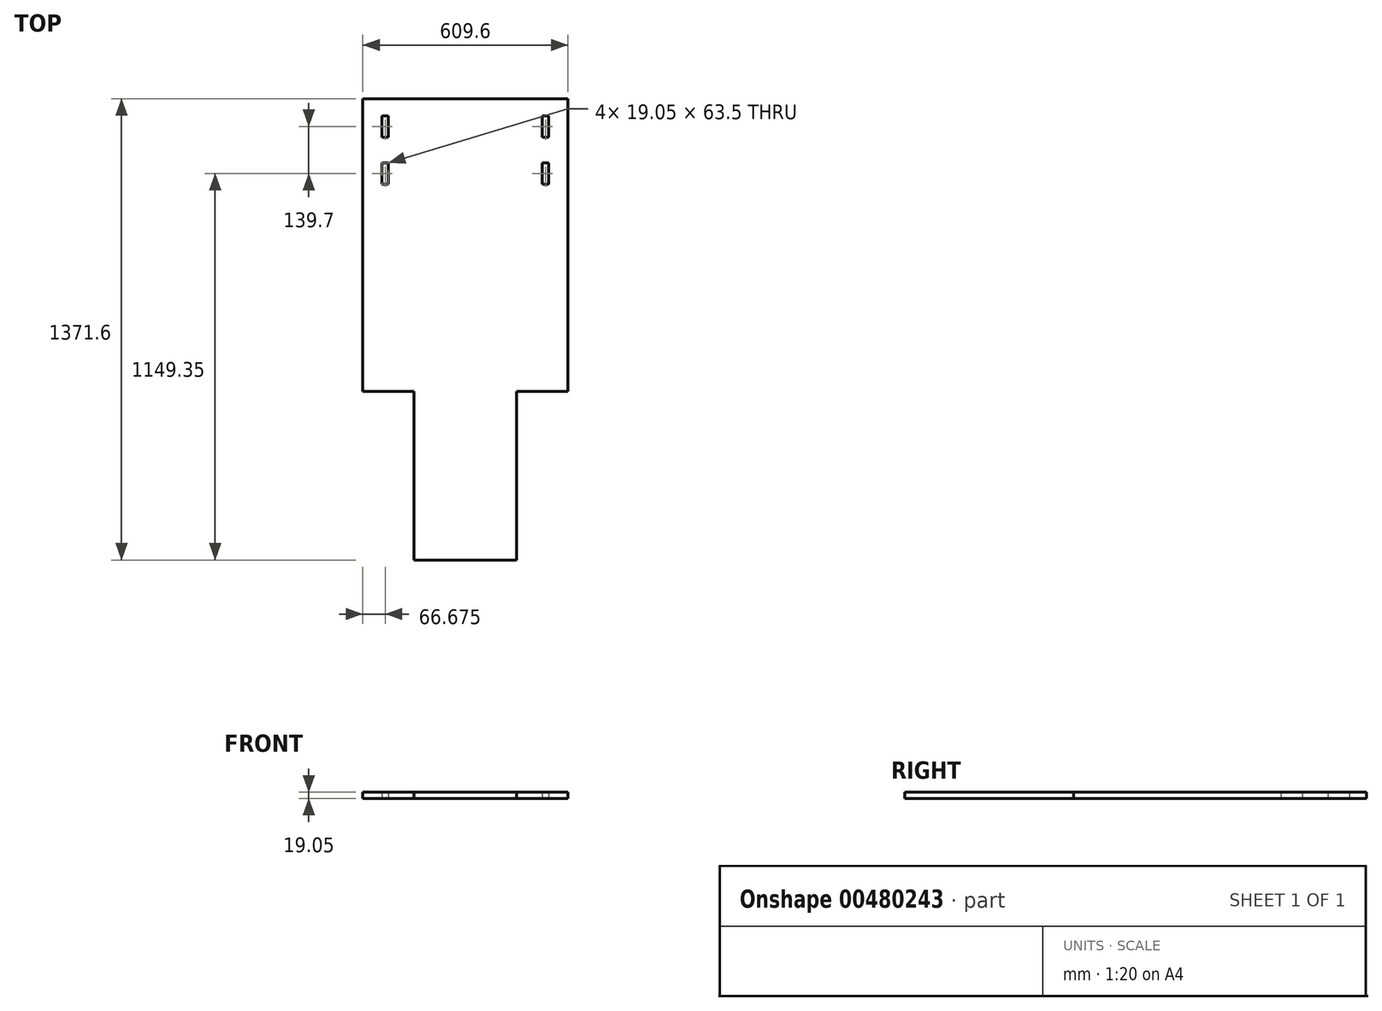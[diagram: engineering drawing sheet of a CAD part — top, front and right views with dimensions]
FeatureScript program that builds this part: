
annotation { "Feature Type Name" : "Feature", "Feature Type Description" : "" }
export const myFeature = defineFeature(function(context is Context, id is Id, definition is map)
    precondition{}
    {
        {
            var Q0;
            Q0=qCreatedBy(makeId("Top.planeOp"),FACE);
            var sketch = newSketch(context, id + "F0", { "sketchPlane" : qUnion([Q0])});
            skLineSegment(sketch, "E0.bottom", {"start": v(0, 0) * mm, "end": v(914.4, 0) * mm});
            skLineSegment(sketch, "E0.top", {"start": v(0, 1371.6) * mm, "end": v(914.4, 1371.6) * mm});
            skLineSegment(sketch, "E0.left", {"start": v(0, 0) * mm, "end": v(0, 1371.6) * mm});
            skLineSegment(sketch, "E0.right", {"start": v(914.4, 0) * mm, "end": v(914.4, 1371.6) * mm});
            skLineSegment(sketch, "E1", {"start": v(0, 0) * mm, "end": v(203.2, 0) * mm});
            skLineSegment(sketch, "E2", {"start": v(203.2, 0) * mm, "end": v(711.2, 0) * mm});
            skLineSegment(sketch, "E3", {"start": v(711.2, 0) * mm, "end": v(914.4, 0) * mm});
            skLineSegment(sketch, "E4", {"start": v(0, 0) * mm, "end": v(0, 304.8) * mm});
            skLineSegment(sketch, "E5", {"start": v(914.4, 304.8) * mm, "end": v(914.4, 0) * mm});
            skLineSegment(sketch, "E6", {"start": v(711.2, 304.8) * mm, "end": v(711.2, 1371.6) * mm, "construction": true});
            skLineSegment(sketch, "E7", {"start": v(203.2, 304.8) * mm, "end": v(203.2, 1371.6) * mm, "construction": true});
            skLineSegment(sketch, "E8", {"start": v(914.4, 1371.6) * mm, "end": v(685.8, 1371.6) * mm, "construction": true});
            skLineSegment(sketch, "E9", {"start": v(685.8, 1371.6) * mm, "end": v(685.8, 1320.8) * mm, "construction": true});
            skLineSegment(sketch, "E10", {"start": v(685.8, 1320.8) * mm, "end": v(685.8, 1257.3) * mm});
            skLineSegment(sketch, "E11", {"start": v(685.8, 1257.3) * mm, "end": v(685.8, 1181.1) * mm, "construction": true});
            skLineSegment(sketch, "E12", {"start": v(685.8, 1181.1) * mm, "end": v(685.8, 1117.6) * mm});
            skLineSegment(sketch, "E13", {"start": v(457.2, 0) * mm, "end": v(457.2, 1371.6) * mm, "construction": true});
            skLineSegment(sketch, "E14.MirrorCS", {"start": v(228.6, 1181.1) * mm, "end": v(228.6, 1117.6) * mm});
            skLineSegment(sketch, "E15.MirrorCS", {"start": v(228.6, 1320.8) * mm, "end": v(228.6, 1257.3) * mm});
            skLineSegment(sketch, "E16", {"start": v(685.8, 1181.1) * mm, "end": v(704.85, 1181.1) * mm});
            skLineSegment(sketch, "E17", {"start": v(704.85, 1181.1) * mm, "end": v(704.85, 1117.6) * mm});
            skLineSegment(sketch, "E18", {"start": v(704.85, 1117.6) * mm, "end": v(685.8, 1117.6) * mm});
            skLineSegment(sketch, "E19.MirrorCS", {"start": v(209.55, 1117.6) * mm, "end": v(228.6, 1117.6) * mm});
            skLineSegment(sketch, "E20.MirrorCS", {"start": v(209.55, 1181.1) * mm, "end": v(209.55, 1117.6) * mm});
            skLineSegment(sketch, "E21.MirrorCS", {"start": v(228.6, 1181.1) * mm, "end": v(209.55, 1181.1) * mm});
            skLineSegment(sketch, "E22", {"start": v(685.8, 1257.3) * mm, "end": v(704.85, 1257.3) * mm});
            skLineSegment(sketch, "E23", {"start": v(704.85, 1257.3) * mm, "end": v(704.85, 1320.8) * mm});
            skLineSegment(sketch, "E24", {"start": v(704.85, 1320.8) * mm, "end": v(685.8, 1320.8) * mm});
            skLineSegment(sketch, "E25.MirrorCS", {"start": v(228.6, 1257.3) * mm, "end": v(209.55, 1257.3) * mm});
            skLineSegment(sketch, "E26.MirrorCS", {"start": v(209.55, 1257.3) * mm, "end": v(209.55, 1320.8) * mm});
            skLineSegment(sketch, "E27.MirrorCS", {"start": v(209.55, 1320.8) * mm, "end": v(228.6, 1320.8) * mm});
            skLineSegment(sketch, "E28.bottom", {"start": v(0, 1371.6) * mm, "end": v(152.4, 1371.6) * mm});
            skLineSegment(sketch, "E28.left", {"start": v(0, 1371.6) * mm, "end": v(0, 1066.8) * mm});
            skLineSegment(sketch, "E29.MirrorCS", {"start": v(914.4, 1371.6) * mm, "end": v(0, 1371.6) * mm});
            skLineSegment(sketch, "E30.MirrorCS", {"start": v(914.4, 1371.6) * mm, "end": v(914.4, 1066.8) * mm});
            skLineSegment(sketch, "E31", {"start": v(304.8, 0) * mm, "end": v(304.8, 501.65) * mm});
            skLineSegment(sketch, "E32", {"start": v(304.8, 501.65) * mm, "end": v(0, 501.65) * mm});
            skLineSegment(sketch, "E33.MirrorCS", {"start": v(609.6, 0) * mm, "end": v(609.6, 501.65) * mm});
            skLineSegment(sketch, "E34.MirrorCS", {"start": v(609.6, 501.65) * mm, "end": v(914.4, 501.65) * mm});
            skLineSegment(sketch, "E35", {"start": v(152.4, 1371.6) * mm, "end": v(152.4, 501.65) * mm});
            skLineSegment(sketch, "E36", {"start": v(762, 501.65) * mm, "end": v(762, 1371.6) * mm});
            skSolve(sketch);
        }
        {
            var Q0;
            Q0=makeQuery(id+"F0.imprint","IMPRINT",FACE,{"disambiguationData":[TD([[makeQuery(id+"F0.imprint","IMPRINT",EDGE,{"derivedFrom":sQuery(id+"F0.wireOp",EDGE,"E10")}),-1.0]])]});
            extrude(context, id + "F1", {"entities" : qUnion([Q0]), "depth" : 19.05 * mm, "offsetDistance" : 25.4 * mm});
        }
    });
